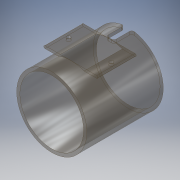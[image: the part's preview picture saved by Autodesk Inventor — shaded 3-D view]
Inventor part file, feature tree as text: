
AUTODESK INVENTOR PART (.ipt)
format: ipt  version: 2019 (Build 230136000, 136)  size: 209,408 bytes
history: native  units: mm
features: extrude x4, sketch x4, projected_geometry x2, plane x1, mirror x1, fillet x1
ambient origin geometry x8: Origin, YZ Plane, XZ Plane, XY Plane, X Axis, Y Axis, Z Axis, Center Point
bodies: Solid1 (feature_tree)
feature tree (13):
  extrude  "Extrusion1"  Depth=100.0mm
  extrude  "Extrusion2"  Depth=30.0mm TaperAngle=0.0deg
  plane  "Work Plane1"
  extrude  "Extrusion3"  Depth=7.0mm TaperAngle=0.0deg
  mirror  "Mirror2"
  fillet  "Fillet1"  Radius=12.0mm
  extrude  "Extrusion4"  Depth=4.0mm
  sketch  "Sketch1"  dims[d0=110.0mm d1=100.0mm]
  sketch  "Sketch2"  dims[d19=120.0mm d20=0.0mm d21=30.0mm d22=0.0mm]
  sketch  "Sketch3"  dims[d23=-60.0mm d27=7.0mm d28=0.0mm d33=12.0mm]
  projected_geometry  "Projected Loop6"
  sketch  "Sketch4"  dims[d43=12.0mm d44=29.0mm d45=4.0mm d46=4.0mm d48=6.0mm d49=5.0mm d50=0.0mm d51=6.0mm]
  projected_geometry  "Projected Loop7"
